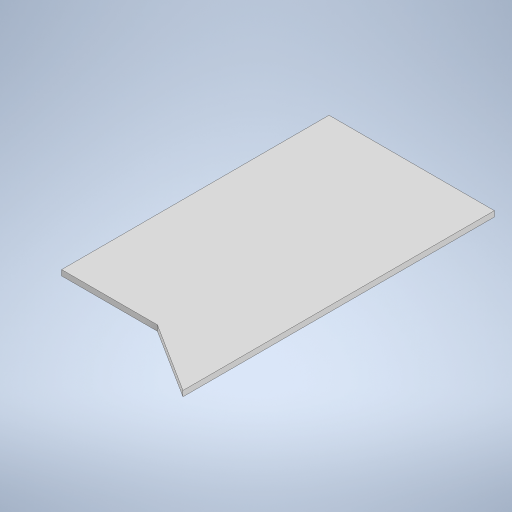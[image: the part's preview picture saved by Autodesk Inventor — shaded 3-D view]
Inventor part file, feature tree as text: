
AUTODESK INVENTOR PART (.ipt)
format: ipt  version: 2024 (Build 280153000, 153)  size: 209,920 bytes
history: native  units: mm
features: extrude x1, sketch x1
ambient origin geometry x8: Origin, YZ Plane, XZ Plane, XY Plane, X Axis, Y Axis, Z Axis, Center Point
bodies: Solid1 (feature_tree)
feature tree (2):
  extrude  "Extrusion1"  Depth=60.0mm
  sketch  "Sketch1"  dims[d0=113.0mm d2=60.0mm d3=2.0mm d4=0.0mm]
